# Revit family: Полуарка — копия
name_source: partatom
category: Осветительные приборы
units: mm (PartAtom-declared; Revit-internal decimal feet)

## family parameters
Всегда вертикально = Да
Источник света = Да
На основе рабочей плоскости = Да
Общий = Нет
При загрузке вырезать с полостями = Нет
Размер круглого соединителя = Использовать диаметр
Тип детали = Нормальный
Точка расчета площади = Нет

## types (1)
- Полуарка — копия
    ADSK_URL страницы изделия = https://www.allfresco.ru
    ADSK_Артикул = ДТУ551
    ADSK_Единица измерения = шт.
    ADSK_Завод-изготовитель = ALFRESCO
    ADSK_Количество фаз = 2
    ADSK_Количество фаз числовое = 0
    ADSK_Коэффициент мощности = 0
    ADSK_Масса = 425
    ADSK_Масса_Текст = 425
    ADSK_Модель = Полуарка ДТУ-55-AF
    ADSK_Наименование = ДТУ551 Светодиодный светильник Полуарка ДТУ-55-AF-180Вт-4840х5630
    ADSK_Напряжение = 220 В
    ADSK_Номинальная мощность = 180 Вт
    ADSK_Полная мощность = 0 В·А
    ADSK_Размер_Высота = 5478 мм
    ADSK_Ток = 0 А
    ADSK_Фактическая мощность = 155 Вт
    ADSK_Энергоэффективность = 100 лм/Вт
    H_вырез = 500 мм
    H_конечной точки = 1300 мм
    H_профиль крепление = 80 мм
    H_профиль светильник = 50 мм
    IP Class = IP 67
    L_отступ до конечной точки = 1550 мм
    L_отступ до центра = 1000 мм
    S_профиль крепление = 190 мм
    S_профиль рассеиватель = 20 мм
    S_профиль светильник = 140 мм
    X_смещение рассеиватель = -80 мм
    angle_обрезка = 20.00°
    h_вырез = 150 мм
    Блок аварийного питания = Нет
    Видимая форма излучения при визуализации = Нет
    Излучение по диаметру окружности = 610 мм
    Класс защиты = 1
    Класс пожароопасности = F (светильники предназначены для установки непосредственно на поверхность из нормально воспламеняемых материалов)
    Климатическая зона = УХЛ1
    Конец_выдавливания = 200 мм
    Конец_выдавливания_1 = 150 мм
    Конец_выдавливания_2 = 160 мм
    Корпус светильника = Антрацит
    Начало_выдавливания = -200 мм
    Начало_выдавливания_1 = -150 мм
    Начало_выдавливания_2 = -160 мм
    Область использования = Парки, скверы, общественные пространства, городская инфраструктура
    Отметка по умолчанию = 1219 мм
    Полная установленная мощность = 0 В·А
    Рассеиватель = Белый_свентодиод
    Светофильтр = 16777215
    Смещение цветовой температуры при затухании лампы = <Нет>
    Таблица выбора = Таблица параметров светильников
    Температура эксплуатации = -40 +50
    Тип ИС = LED-модуль
    Тип КСС = тип Д (косинусная)
    Тип ПРА = -
    Тип продукции = LED-светильник
    Угол наклона = 135.00°
    Файл фотометрической сетки = Poluarka DTU-55-AF 180W.ies
    Цветоывая температура = 2700-5500

## geometry (parser evidence)
native form markers: Blend x4
no freeform markers — native parametric forms only
